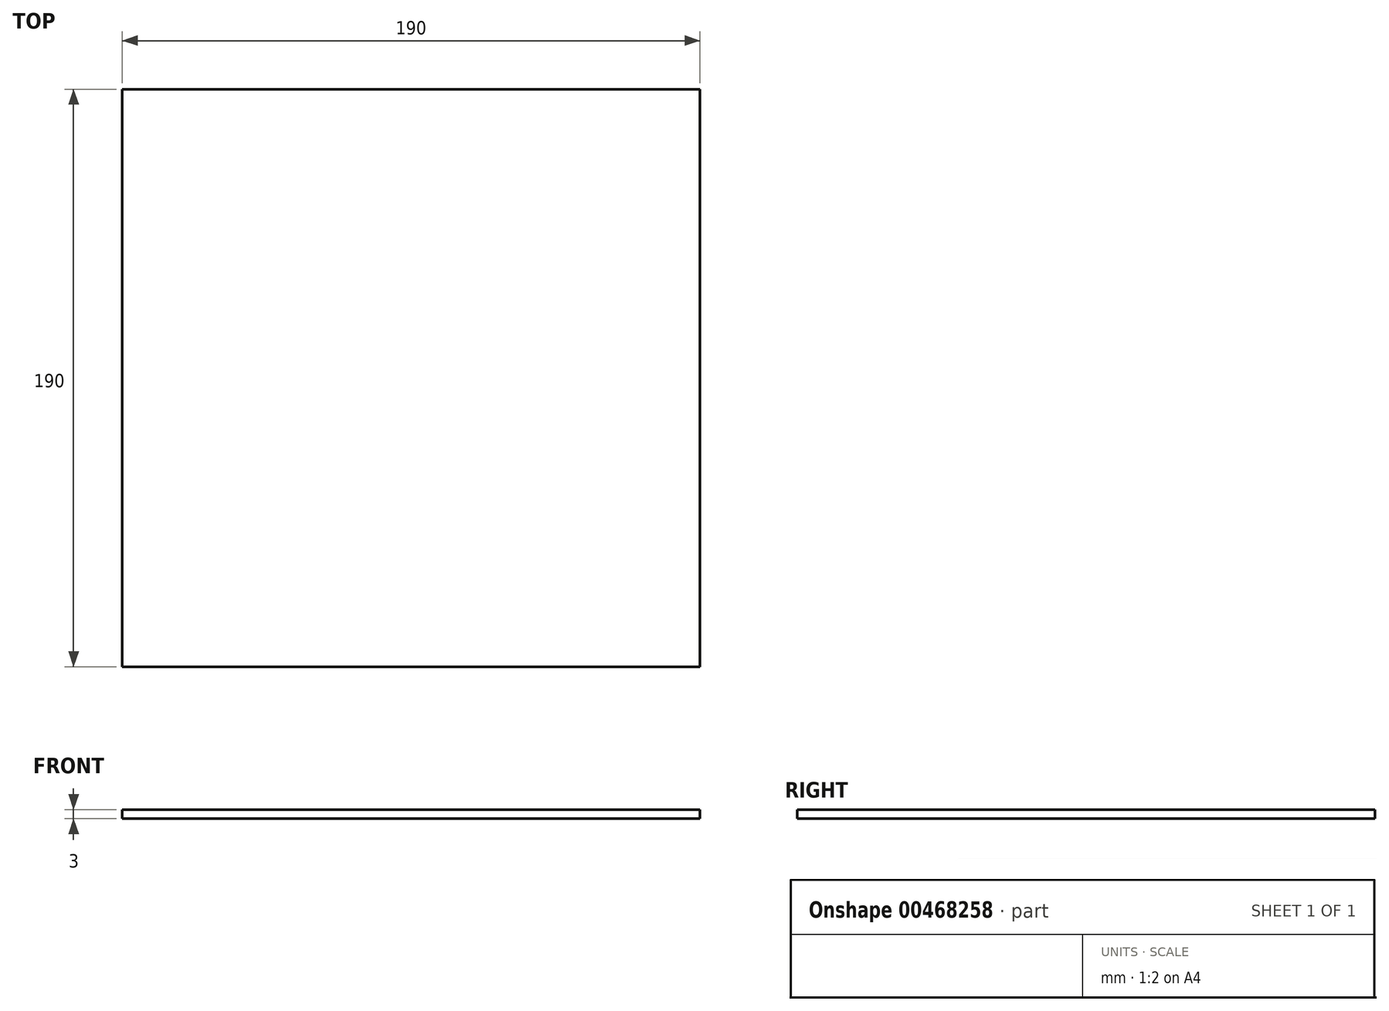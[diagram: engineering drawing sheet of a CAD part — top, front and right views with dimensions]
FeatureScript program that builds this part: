
annotation { "Feature Type Name" : "Feature", "Feature Type Description" : "" }
export const myFeature = defineFeature(function(context is Context, id is Id, definition is map)
    precondition{}
    {
        {
            var Q0;
            Q0=qCreatedBy(makeId("Top.planeOp"),FACE);
            var sketch = newSketch(context, id + "F0", { "sketchPlane" : qUnion([Q0])});
            skLineSegment(sketch, "E0.bottom", {"start": v(95, -95) * mm, "end": v(-95, -95) * mm});
            skLineSegment(sketch, "E0.top", {"start": v(95, 95) * mm, "end": v(-95, 95) * mm});
            skLineSegment(sketch, "E0.left", {"start": v(95, -95) * mm, "end": v(95, 95) * mm});
            skLineSegment(sketch, "E0.right", {"start": v(-95, -95) * mm, "end": v(-95, 95) * mm});
            skPoint(sketch, "E0.middle", {"position": v(0, 0) * mm});
            skSolve(sketch);
        }
        {
            var Q0;
            Q0 = qSketchRegion(id + "F0", true);
            extrude(context, id + "F1", {"entities" : qUnion([Q0]), "depth" : 3 * mm});
        }
    });
